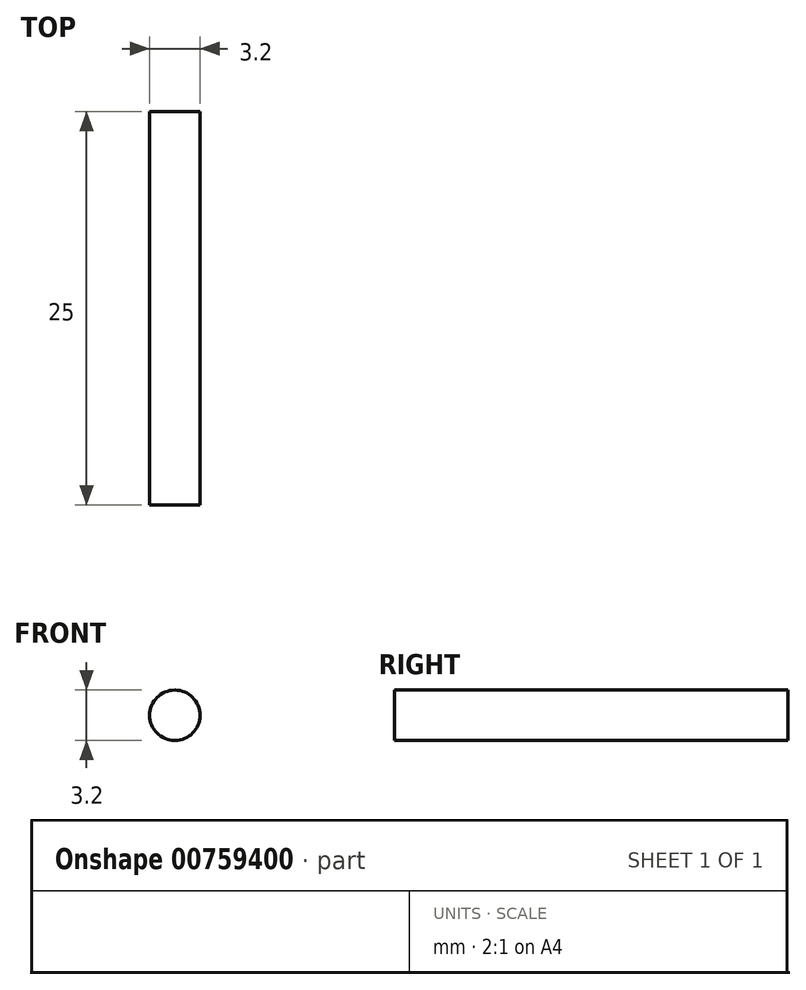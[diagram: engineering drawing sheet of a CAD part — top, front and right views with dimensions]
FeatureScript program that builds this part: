
annotation { "Feature Type Name" : "Feature", "Feature Type Description" : "" }
export const myFeature = defineFeature(function(context is Context, id is Id, definition is map)
    precondition{}
    {
        {
            var Q0;
            Q0=qCreatedBy(makeId("Front.planeOp"),FACE);
            var sketch = newSketch(context, id + "F0", { "sketchPlane" : qUnion([Q0])});
            skCircle(sketch, "E0", {"center": v(0, 0) * mm, "radius": 1.6 * mm});
            skSolve(sketch);
        }
        {
            var Q0;
            Q0 = qSketchRegion(id + "F0", true);
            extrude(context, id + "F1", {"entities" : qUnion([Q0]), "depth" : 25 * mm, "offsetDistance" : 25 * mm});
        }
    });
